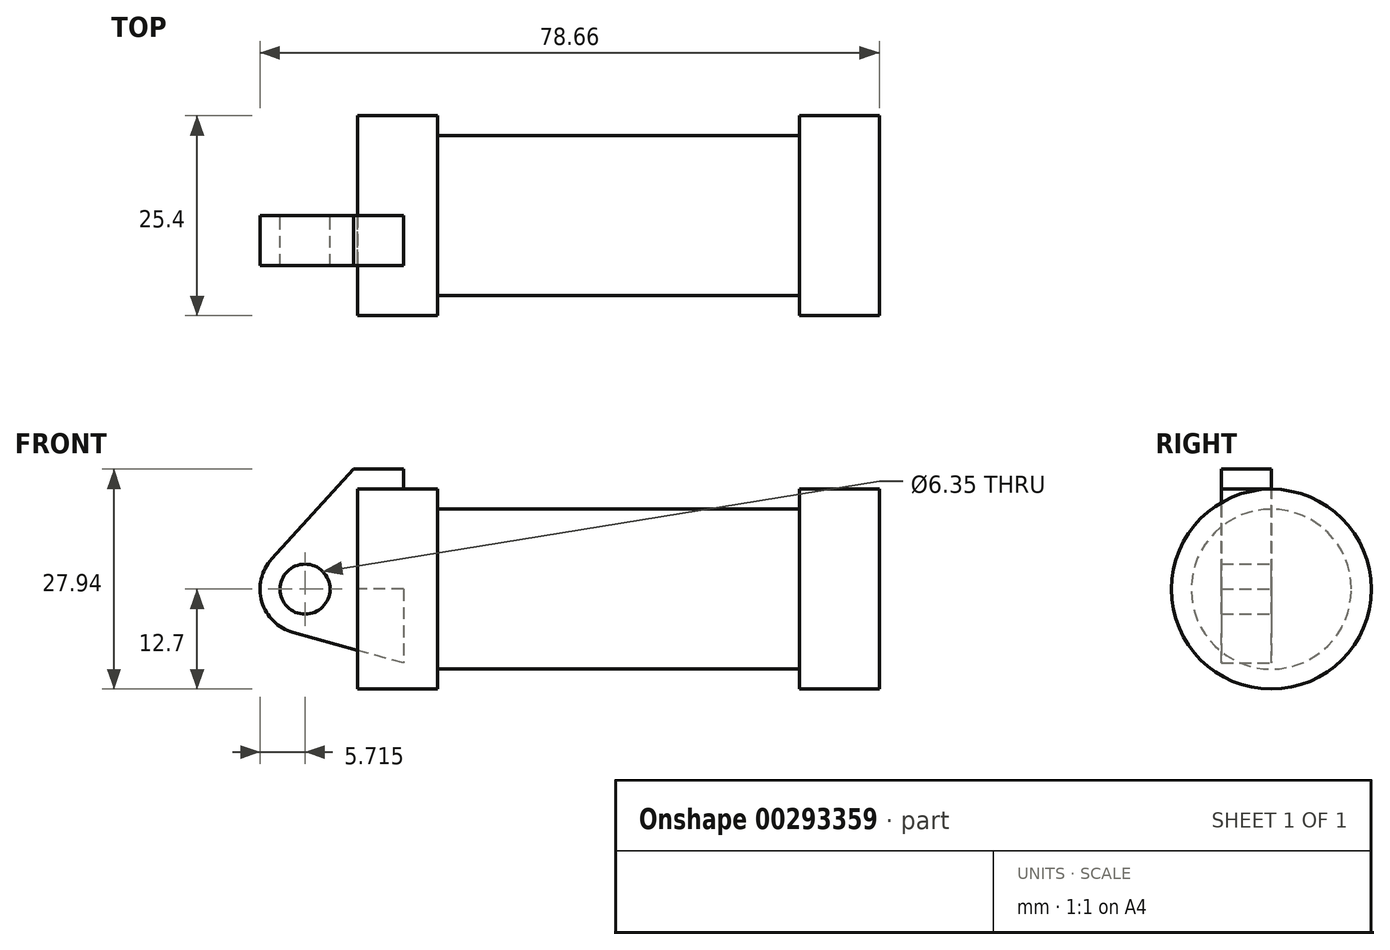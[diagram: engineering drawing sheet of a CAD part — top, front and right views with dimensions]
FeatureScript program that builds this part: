
annotation { "Feature Type Name" : "Feature", "Feature Type Description" : "" }
export const myFeature = defineFeature(function(context is Context, id is Id, definition is map)
    precondition{}
    {
        {
            var Q0;
            Q0=qCreatedBy(makeId("Front.planeOp"),FACE);
            var sketch = newSketch(context, id + "F0", { "sketchPlane" : qUnion([Q0])});
            skLineSegment(sketch, "E0", {"start": v(0, 0) * mm, "end": v(0, 12.7) * mm});
            skLineSegment(sketch, "E1", {"start": v(0, 12.7) * mm, "end": v(10.16, 12.7) * mm});
            skLineSegment(sketch, "E2", {"start": v(10.16, 12.7) * mm, "end": v(10.16, 10.16) * mm});
            skLineSegment(sketch, "E3", {"start": v(10.16, 10.16) * mm, "end": v(56.13, 10.16) * mm});
            skLineSegment(sketch, "E4", {"start": v(56.13, 10.16) * mm, "end": v(56.13, 12.7) * mm});
            skLineSegment(sketch, "E5", {"start": v(56.13, 12.7) * mm, "end": v(66.3, 12.7) * mm});
            skLineSegment(sketch, "E6", {"start": v(66.3, 12.7) * mm, "end": v(66.3, 0) * mm});
            skLineSegment(sketch, "E7", {"start": v(66.3, 0) * mm, "end": v(0, 0) * mm});
            skLineSegment(sketch, "E8", {"start": v(5.84, 15.24) * mm, "end": v(-0.5, 15.24) * mm});
            skLineSegment(sketch, "E9", {"start": v(-0.5, 15.24) * mm, "end": v(-10.88, 3.85) * mm});
            skLineSegment(sketch, "E10", {"start": v(0, 0) * mm, "end": v(-6.65, 0) * mm});
            skCircle(sketch, "E11", {"center": v(-6.65, 0) * mm, "radius": 5.72 * mm});
            skCircle(sketch, "E12", {"center": v(-6.65, 0) * mm, "radius": 3.18 * mm});
            skLineSegment(sketch, "E13", {"start": v(5.84, 15.24) * mm, "end": v(5.84, -9.4) * mm});
            skLineSegment(sketch, "E14", {"start": v(5.84, -9.4) * mm, "end": v(-8.18, -5.5) * mm});
            skSolve(sketch);
        }
        {
            var Q0;
            {var subQ0=sQuery(id+"F0.wireOp",EDGE,"E2");Q0=makeQuery(id+"F0.imprint","IMPRINT",FACE,{"disambiguationData":[TD([[makeQuery(id+"F0.imprint","IMPRINT",EDGE,{"derivedFrom":subQ0}),-1.0]])]});}
            var Q1;
            {var subQ0=sQuery(id+"F0.wireOp",EDGE,"E0");Q1=makeQuery(id+"F0.imprint","IMPRINT",FACE,{"disambiguationData":[TD([[makeQuery(id+"F0.imprint","IMPRINT",EDGE,{"derivedFrom":subQ0}),-1.0]])]});}
            var Q2;
            Q2=sQuery(id+"F0.wireOp",EDGE,"E7");
            revolve(context, id + "F1", {"entities" : qUnion([Q0, Q1]), "axis" : qUnion([Q2]), "revolveType" : RevolveType.FULL});
        }
        {
            var Q0;
            {var subQ1=sQuery(id+"F0.wireOp",EDGE,"E0");Q0=makeQuery(id+"F0.imprint","IMPRINT",FACE,{"disambiguationData":[TD([[makeQuery(id+"F0.imprint","IMPRINT",EDGE,{"derivedFrom":subQ1}),1.0]])]});}
            var Q1;
            Q1=makeQuery(id+"F0.imprint","IMPRINT",FACE,{"disambiguationData":[TD([[makeQuery(id+"F0.imprint","IMPRINT",EDGE,{"derivedFrom":sQuery(id+"F0.wireOp",EDGE,"E12")}),-1.0]])]});
            var Q2;
            {var subQ0=sQuery(id+"F0.wireOp",EDGE,"E14");Q2=makeQuery(id+"F0.imprint","IMPRINT",FACE,{"disambiguationData":[TD([[makeQuery(id+"F0.imprint","IMPRINT",EDGE,{"derivedFrom":subQ0}),-1.0]])]});}
            extrude(context, id + "F2", {"entities" : qUnion([Q0, Q1, Q2]), "depth" : 6.35 * mm});
        }
    });
